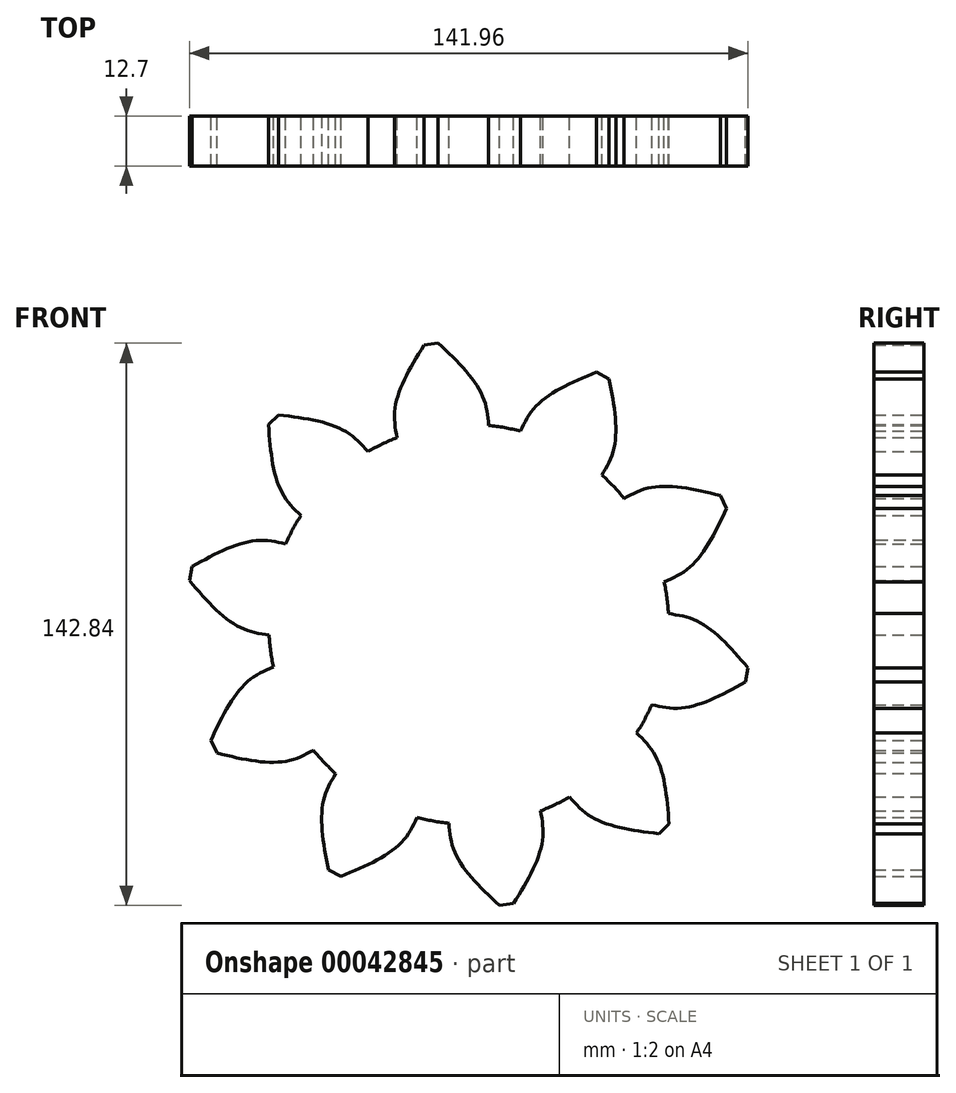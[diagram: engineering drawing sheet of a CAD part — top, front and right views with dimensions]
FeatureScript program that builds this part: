
annotation { "Feature Type Name" : "Feature", "Feature Type Description" : "" }
export const myFeature = defineFeature(function(context is Context, id is Id, definition is map)
    precondition{}
    {
        {
            var Q0;
            Q0=qCreatedBy(makeId("Front.planeOp"),FACE);
            var sketch = newSketch(context, id + "F0", { "sketchPlane" : qUnion([Q0])});
            skCircle(sketch, "E0", {"center": v(0, 0) * mm, "radius": 50.8 * mm});
            skLineSegment(sketch, "E1", {"start": v(0, 50.8) * mm, "end": v(0, 63.5) * mm, "construction": true});
            skLineSegment(sketch, "E2", {"start": v(0, 63.5) * mm, "end": v(-30.48, 40.64) * mm, "construction": true});
            skLineSegment(sketch, "E3", {"start": v(-39.6, 31.8) * mm, "end": v(-7.8, 71.42) * mm, "construction": true});
            skLineSegment(sketch, "E4", {"start": v(-19.45, 46.93) * mm, "end": v(4.02, 56.65) * mm, "construction": true});
            skFitSpline(sketch, "E5", {"points": [v(5.06, 50.55) * mm, v(4.02, 56.65) * mm, v(0, 63.5) * mm, v(-7.8, 71.42) * mm], "startDerivative": vector(-1.87, 21.29) * mm, "endDerivative": vector(-21.83, 20.41) * mm});
            skLineSegment(sketch, "E6", {"start": v(-7.8, 71.42) * mm, "end": v(-5.51, 50.5) * mm, "construction": true});
            skLineSegment(sketch, "E7", {"start": v(-6.77, 50.35) * mm, "end": v(-9.58, 71.2) * mm, "construction": true});
            skFitSpline(sketch, "E8.MirrorCS", {"points": [v(-18.24, 47.41) * mm, v(-18.85, 53.58) * mm, v(-16.79, 61.24) * mm, v(-11.36, 70.94) * mm], "startDerivative": vector(-3.83, 21.02) * mm, "endDerivative": vector(15.66, 25.46) * mm});
            skLineSegment(sketch, "E9", {"start": v(-11.36, 70.94) * mm, "end": v(-7.8, 71.42) * mm});
            skLineSegment(sketch, "E10.anchor1", {"start": v(0, 0) * mm, "end": v(-11.36, 70.94) * mm, "construction": true});
            skLineSegment(sketch, "E10.anchor2", {"start": v(0, 0) * mm, "end": v(-11.36, 70.94) * mm, "construction": true});
            skSolve(sketch);
        }
        {
            var Q0;
            {var subQ0=sQuery(id+"F0.wireOp",EDGE,"E0");var subQ2=makeQuery(id+"F0.imprint","INTERSECT",VERTEX,{"derivedFrom":[subQ0,sQuery(id+"F0.wireOp",EDGE,"E5")]});Q0=makeQuery(id+"F0.imprint","IMPRINT",FACE,{"disambiguationData":[TD([[makeQuery(id+"F0.imprint","IMPRINT",EDGE,{"disambiguationData":[TD([[subQ2,-1.0]])],"derivedFrom":subQ0}),1.0]])]});}
            extrude(context, id + "F1", {"entities" : qUnion([Q0]), "depth" : 12.7 * mm});
        }
        {
            var Q0;
            {var subQ1=sQuery(id+"F0.wireOp",EDGE,"E5");Q0=makeQuery(id+"F0.imprint","IMPRINT",FACE,{"disambiguationData":[TD([[makeQuery(id+"F0.imprint","IMPRINT",EDGE,{"derivedFrom":subQ1}),1.0]])]});}
            var Q1;
            Q1=makeQuery(id+"F1.opExtrude","CAP_FACE",FACE,{"disambiguationData":[OSD([sQuery(id+"F0.wireOp",EDGE,"E0")])],"isStart":false});
            extrude(context, id + "F2", {"entities" : qUnion([Q0]), "endBound" : BoundingType.UP_TO_SURFACE, "endBoundEntityFace" : qUnion([Q1]), "depth" : 12.7 * mm});
        }
        {
            var Q0;
            Q0=qCreatedBy(makeId("Top.planeOp"),FACE);
            var sketch = newSketch(context, id + "F3", { "sketchPlane" : qUnion([Q0])});
            skLineSegment(sketch, "E11", {"start": v(0, 0) * mm, "end": v(0, -20.65) * mm, "construction": true});
            skSolve(sketch);
        }
        {
            var Q0;
            Q0=makeQuery(id+"F2.opExtrude","SWEPT_BODY",BODY,{"disambiguationData":[OSD([sQuery(id+"F0.wireOp",EDGE,"E0"),sQuery(id+"F0.wireOp",EDGE,"E5"),sQuery(id+"F0.wireOp",EDGE,"E8.MirrorCS"),sQuery(id+"F0.wireOp",EDGE,"E9")])]});
            var Q1;
            Q1=sQuery(id+"F3.wireOp",EDGE,"E11");
            circularPattern(context, id + "F4", {"operationType" : NewBodyOperationType.ADD, "entities" : qUnion([Q0]), "axis" : qUnion([Q1]), "angle" : 360 * degree, "instanceCount" : 10, "equalSpace" : true});
        }
    });
